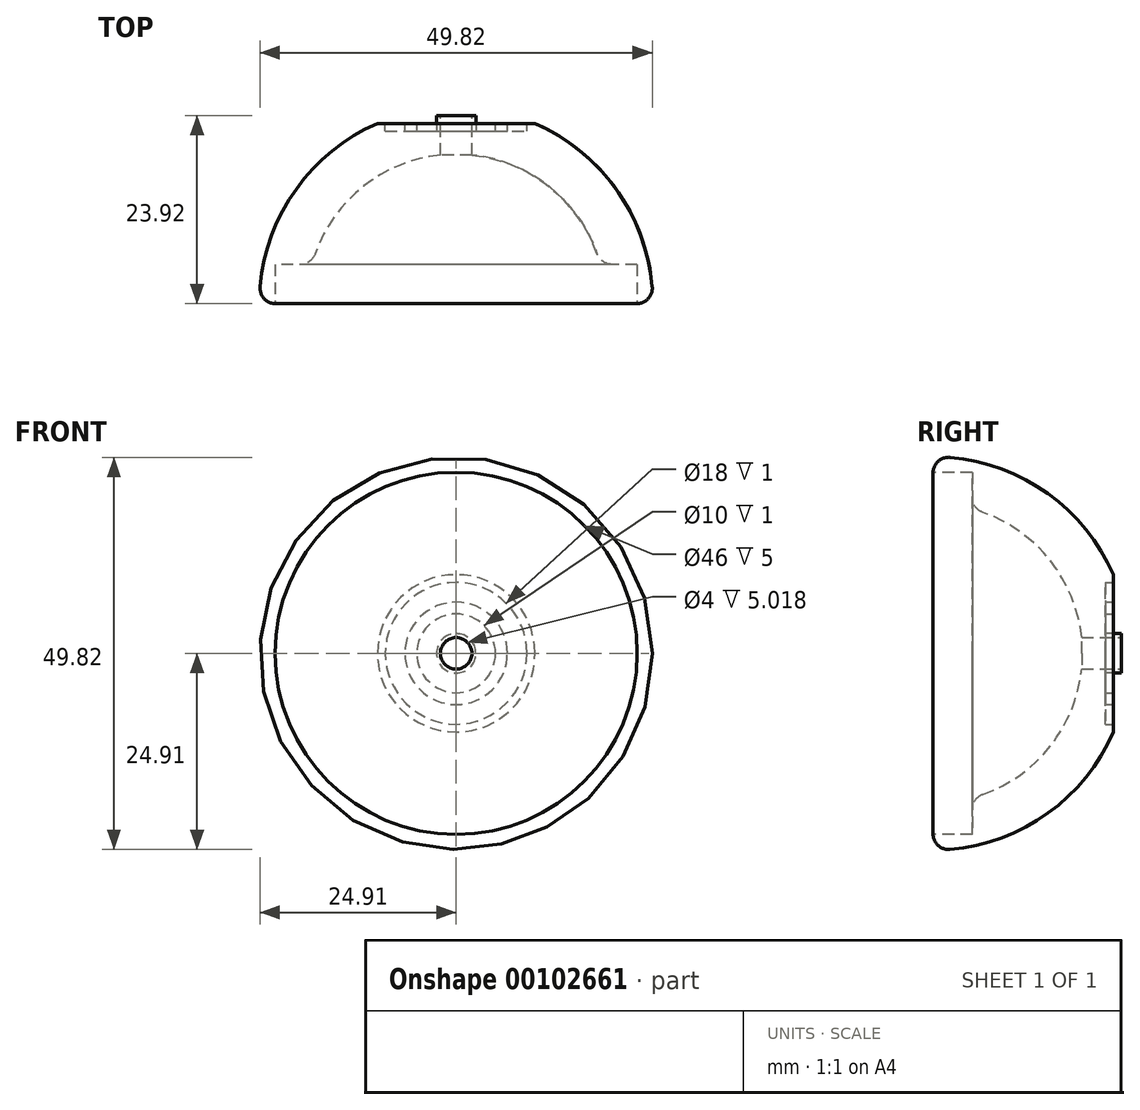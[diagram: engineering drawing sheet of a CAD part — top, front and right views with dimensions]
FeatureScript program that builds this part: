
annotation { "Feature Type Name" : "Feature", "Feature Type Description" : "" }
export const myFeature = defineFeature(function(context is Context, id is Id, definition is map)
    precondition{}
    {
        {
            var Q0;
            Q0=qCreatedBy(makeId("Top.planeOp"),FACE);
            var sketch = newSketch(context, id + "F0", { "sketchPlane" : qUnion([Q0])});
            skLineSegment(sketch, "E0", {"start": v(-45.07, -4.07) * mm, "end": v(4.93, -4.07) * mm, "construction": true});
            skArc(sketch, "E1", {"start": v(-45.07, -4.07) * mm, "mid": v(-20.07, 20.93) * mm, "end": v(4.93, -4.07) * mm});
            skLineSegment(sketch, "E2", {"start": v(-30.07, 18.85) * mm, "end": v(-10.07, 18.85) * mm});
            skLineSegment(sketch, "E3", {"start": v(-45.07, -4.07) * mm, "end": v(-39.07, -4.07) * mm});
            skLineSegment(sketch, "E4", {"start": v(4.93, -4.07) * mm, "end": v(-1.07, -4.07) * mm});
            skArc(sketch, "E5", {"start": v(-39.07, -4.07) * mm, "mid": v(-20.07, 14.93) * mm, "end": v(-1.07, -4.07) * mm});
            skLineSegment(sketch, "E6", {"start": v(-30.07, 12.09) * mm, "end": v(-10.07, 12.09) * mm});
            skLineSegment(sketch, "E7", {"start": v(-20.07, -4.07) * mm, "end": v(-20.07, 22.97) * mm});
            skPoint(sketch, "E7.endSnap0", {"position": v(-20.07, 20.93) * mm});
            skSolve(sketch);
        }
        {
            var Q0;
            {var subQ1=sQuery(id+"F0.wireOp",EDGE,"E3");Q0=makeQuery(id+"F0.imprint","IMPRINT",FACE,{"disambiguationData":[TD([[makeQuery(id+"F0.imprint","IMPRINT",EDGE,{"derivedFrom":subQ1}),1.0]])]});}
            var Q1;
            {var subQ0=sQuery(id+"F0.wireOp",EDGE,"E6");var subQ1=sQuery(id+"F0.wireOp",EDGE,"E5");var subQ2=makeQuery(id+"F0.imprint","INTERSECT",VERTEX,{"disambiguationData":[OD(0.0)],"derivedFrom":[subQ1,subQ0]});Q1=makeQuery(id+"F0.imprint","IMPRINT",FACE,{"disambiguationData":[TD([[makeQuery(id+"F0.imprint","IMPRINT",EDGE,{"disambiguationData":[TD([[subQ2,-1.0]])],"derivedFrom":subQ1}),-1.0]])]});}
            var Q2;
            Q2=sQuery(id+"F0.wireOp",EDGE,"E7");
            revolve(context, id + "F1", {"entities" : qUnion([Q0, Q1]), "axis" : qUnion([Q2]), "revolveType" : RevolveType.FULL});
        }
        {
            var Q0;
            Q0=makeQuery(id+"F1.opRevolve","SWEPT_FACE",FACE,{"disambiguationData":[OSD([sQuery(id+"F0.wireOp",EDGE,"E2")])]});
            var sketch = newSketch(context, id + "F2", { "sketchPlane" : qUnion([Q0])});
            skPoint(sketch, "E8", {"position": v(20.07, 0) * mm});
            skCircle(sketch, "E9", {"center": v(20.07, 0) * mm, "radius": 9 * mm});
            skCircle(sketch, "E10", {"center": v(20.07, 0) * mm, "radius": 6.5 * mm});
            skSolve(sketch);
        }
        {
            var Q0;
            Q0 = qSketchRegion(id + "F2", true);
            extrude(context, id + "F3", {"entities" : qUnion([Q0]), "operationType" : NewBodyOperationType.REMOVE, "oppositeDirection" : true, "depth" : 1 * mm});
        }
        {
            var Q0;
            Q0=makeQuery(id+"F3.boolean.opBoolean","SPLIT",FACE,{"disambiguationData":[TD([makeQuery(id+"F3.opExtrude","SWEPT_FACE",FACE,{"disambiguationData":[OSD([sQuery(id+"F2.wireOp",EDGE,"E10")])]})])],"derivedFrom":makeQuery(id+"F1.opRevolve","SWEPT_FACE",FACE,{"disambiguationData":[OSD([sQuery(id+"F0.wireOp",EDGE,"E2")])]})});
            var sketch = newSketch(context, id + "F4", { "sketchPlane" : qUnion([Q0])});
            skPoint(sketch, "E11", {"position": v(20.07, 0) * mm});
            skCircle(sketch, "E12", {"center": v(20.07, 0) * mm, "radius": 5 * mm});
            skSolve(sketch);
        }
        {
            var Q0;
            Q0 = qSketchRegion(id + "F4", true);
            extrude(context, id + "F5", {"entities" : qUnion([Q0]), "operationType" : NewBodyOperationType.REMOVE, "oppositeDirection" : true, "depth" : 1 * mm});
        }
        {
            var Q0;
            Q0=makeQuery(id+"F1.opRevolve","SWEPT_FACE",FACE,{"disambiguationData":[OSD([sQuery(id+"F0.wireOp",EDGE,"E3")])]});
            var sketch = newSketch(context, id + "F6", { "sketchPlane" : qUnion([Q0])});
            skPoint(sketch, "E13", {"position": v(-20.07, 0) * mm});
            skCircle(sketch, "E14", {"center": v(-20.07, 0) * mm, "radius": 23 * mm});
            skSolve(sketch);
        }
        {
            var Q0;
            Q0 = qSketchRegion(id + "F6", true);
            extrude(context, id + "F7", {"entities" : qUnion([Q0]), "operationType" : NewBodyOperationType.REMOVE, "oppositeDirection" : true, "depth" : 5 * mm});
        }
        {
            var Q0;
            Q0=makeQuery(id+"F5.boolean.opBoolean","COPY",FACE,{"derivedFrom":makeQuery(id+"F5.opExtrude","CAP_FACE",FACE,{"disambiguationData":[OSD([sQuery(id+"F4.wireOp",EDGE,"E12")])],"isStart":false})});
            var sketch = newSketch(context, id + "F8", { "sketchPlane" : qUnion([Q0])});
            skPoint(sketch, "E15", {"position": v(20.07, 0) * mm});
            skCircle(sketch, "E16", {"center": v(20.07, 0) * mm, "radius": 2.5 * mm});
            skSolve(sketch);
        }
        {
            var Q0;
            Q0 = qSketchRegion(id + "F8", true);
            extrude(context, id + "F9", {"entities" : qUnion([Q0]), "operationType" : NewBodyOperationType.ADD, "depth" : 2 * mm});
        }
        {
            var Q0;
            Q0=makeQuery(id+"F9.opExtrude","CAP_FACE",FACE,{"disambiguationData":[OSD([sQuery(id+"F8.wireOp",EDGE,"E16")])],"isStart":false});
            var sketch = newSketch(context, id + "F10", { "sketchPlane" : qUnion([Q0])});
            skPoint(sketch, "E17", {"position": v(20.07, 0) * mm});
            skCircle(sketch, "E18", {"center": v(20.07, 0) * mm, "radius": 2 * mm});
            skSolve(sketch);
        }
        {
            var Q0;
            Q0 = qSketchRegion(id + "F10", true);
            extrude(context, id + "F11", {"entities" : qUnion([Q0]), "operationType" : NewBodyOperationType.REMOVE, "oppositeDirection" : true, "depth" : 25 * mm});
        }
        {
            var Q0;
            Q0=makeQuery(id+"F1.opRevolve","SWEPT_EDGE",EDGE,{"disambiguationData":[OSD([sQuery(id+"F0.wireOp",EDGE,"E1"),sQuery(id+"F0.wireOp",EDGE,"E3")])]});
            var Q1;
            Q1=makeQuery(id+"F1.opRevolve","SWEPT_EDGE",EDGE,{"disambiguationData":[OSD([sQuery(id+"F0.wireOp",EDGE,"E5"),sQuery(id+"F0.wireOp",EDGE,"E6")])]});
            var Q2;
            Q2=makeQuery(id+"F7.boolean.opBoolean","INTERSECT",EDGE,{"derivedFrom":[makeQuery(id+"F1.opRevolve","SWEPT_FACE",FACE,{"disambiguationData":[OSD([sQuery(id+"F0.wireOp",EDGE,"E5")])]}),makeQuery(id+"F7.opExtrude","CAP_FACE",FACE,{"disambiguationData":[OSD([sQuery(id+"F6.wireOp",EDGE,"E14")])],"isStart":false})]});
            fillet(context, id + "F12", {"entities" : qUnion([Q0, Q1, Q2]), "radius" : 2 * mm, "tangentPropagation" : true, "allowEdgeOverflow" : false});
        }
    });
